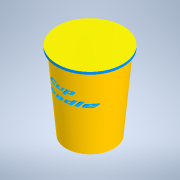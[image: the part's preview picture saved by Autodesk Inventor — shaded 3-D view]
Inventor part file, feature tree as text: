
AUTODESK INVENTOR PART (.ipt)
format: ipt  version: 2020 (Build 240168000, 168)  size: 453,632 bytes
history: native  units: in
note: dims shown in document units (in); Inventor stores cm internally (conversion verified against a paired STEP export)
features: sketch x3, extrude x2, revolve x1
ambient origin geometry x8: Origin, YZ Plane, XZ Plane, XY Plane, X Axis, Y Axis, Z Axis, Center Point
bodies: Solid1 (feature_tree)
feature tree (6):
  revolve  "Revolution1"  [1 undecoded]
  extrude  "Extrusion1"  Depth=1.8307in
  extrude  "Extrusion2"  Depth=0.25in
  sketch  "Sketch1"  dims[d0=1.3189in d1=0.0in]
  sketch  "Sketch2"  dims[d2=4.3307in d3=1.8307in]
  sketch  "Sketch3"  dims[d4=0.1378in d5=0.1378in d6=90.0deg d7=1.75in d8=0.0in d9=0.25in d10=0.0in]
note: 1 required parameter value undecoded (feature->parameter linkage not recoverable at this tier; creation-order binding heuristic only, values carry confidence <= 0.55)
